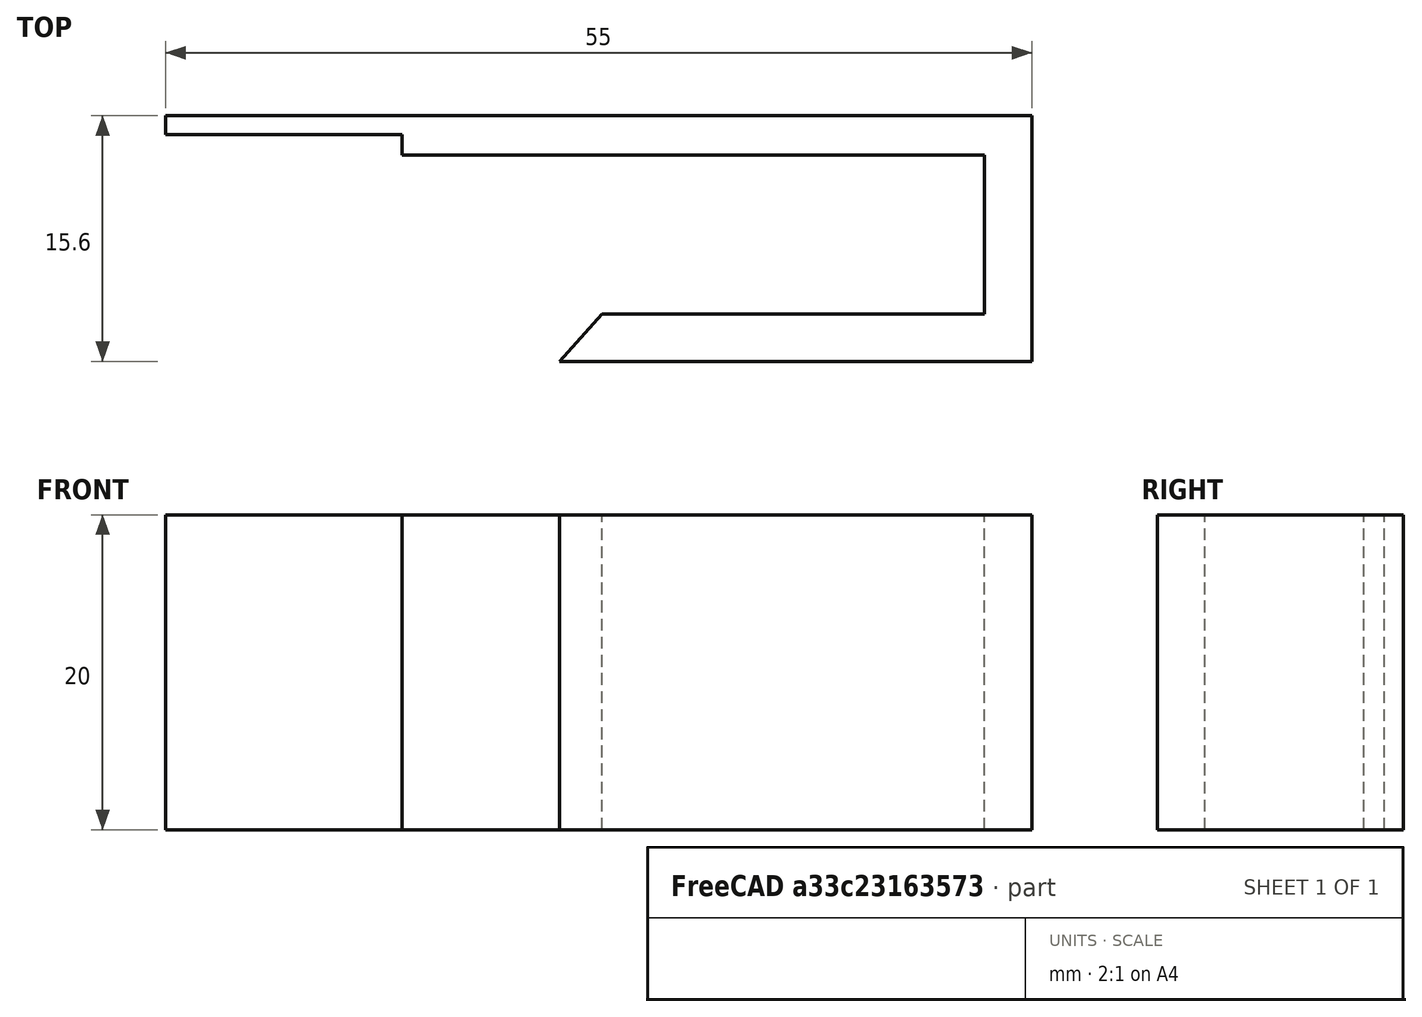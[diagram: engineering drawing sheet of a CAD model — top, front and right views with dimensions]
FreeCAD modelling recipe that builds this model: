
FCSTD DOCUMENT  (FreeCAD 0.15R4671 (Git))
Label: heaterBracketHighFixedWidth
License: CC-BY 3.0
LicenseURL: http://creativecommons.org/licenses/by/3.0/
objects: Sketcher::SketchObject×1, PartDesign::Pad×1
note: 3 computed .brp shape members not serialized (recipe doc carries the construction recipe); baked Part::Feature solids carry a one-line shape summary decoded from their .brp

FEATURE [Sketcher::SketchObject] Sketch  label="Profil"
  sketch-geometry (11):
    g0: LineSegment StartX=0 StartY=71 StartZ=0 EndX=-7 EndY=71 EndZ=0
    g1: LineSegment StartX=-40 StartY=22.5 StartZ=0 EndX=-3 EndY=22.5 EndZ=0
    g2: LineSegment StartX=-3 StartY=22.5 StartZ=0 EndX=-3 EndY=12.4 EndZ=0
    g3: LineSegment StartX=-3 StartY=12.4 StartZ=0 EndX=-27.2936 EndY=12.4 EndZ=0
    g4: LineSegment StartX=-27.2936 StartY=12.4 StartZ=0 EndX=-30 EndY=9.4 EndZ=0
    g5: LineSegment StartX=-30 StartY=9.4 StartZ=0 EndX=0 EndY=9.4 EndZ=0
    g6: LineSegment StartX=0 StartY=25 StartZ=0 EndX=-55 EndY=25 EndZ=0
    g7: LineSegment StartX=0 StartY=25 StartZ=0 EndX=0 EndY=9.4 EndZ=0
    g8: LineSegment StartX=-55 StartY=25 StartZ=0 EndX=-55 EndY=23.8 EndZ=0
    g9: LineSegment StartX=-55 StartY=23.8 StartZ=0 EndX=-40 EndY=23.8 EndZ=0
    g10: LineSegment StartX=-40 StartY=23.8 StartZ=0 EndX=-40 EndY=22.5 EndZ=0
  constraints (29):
    c: Horizontal(g0)
    c: DistanceX(g0) = -7
    c: Horizontal(g1)
    c: Vertical(g2)
    c: Coincident(g2,g3)
    c: Coincident(g3,g4)
    c: Coincident(g4,g5)
    c: Coincident(g1,g2)
    c: DistanceY(g6,g1) = -2.5
    c: Horizontal(g6)
    c: DistanceX(g-1,g2) = -3
    c: Coincident(g6,g7)
    c: Coincident(g5,g7)
    c: DistanceX(g-1,g6) = -55
    c: DistanceY(g-1,g6) = 25
    c: DistanceX(g6,g1) = 15
    c: Coincident(g8,g9)
    c: Coincident(g9,g10)
    c: Coincident(g1,g10)
    c: Coincident(g6,g8)
    c: Vertical(g8)
    c: Vertical(g10)
    c: DistanceY(g10) = -1.3
    c: Horizontal(g9)
    c: DistanceY(g1,g3) = -10.1
    c: DistanceY(g5,g2) = 3
    c: DistanceX(g4,g5) = 30
    c: Horizontal(g3)
    c: Horizontal(g5)
FEATURE [PartDesign::Pad] Pad  label="Corps"
  Length = 20
  Length2 = 100
  Sketch = -> Sketch
  Type = 0
